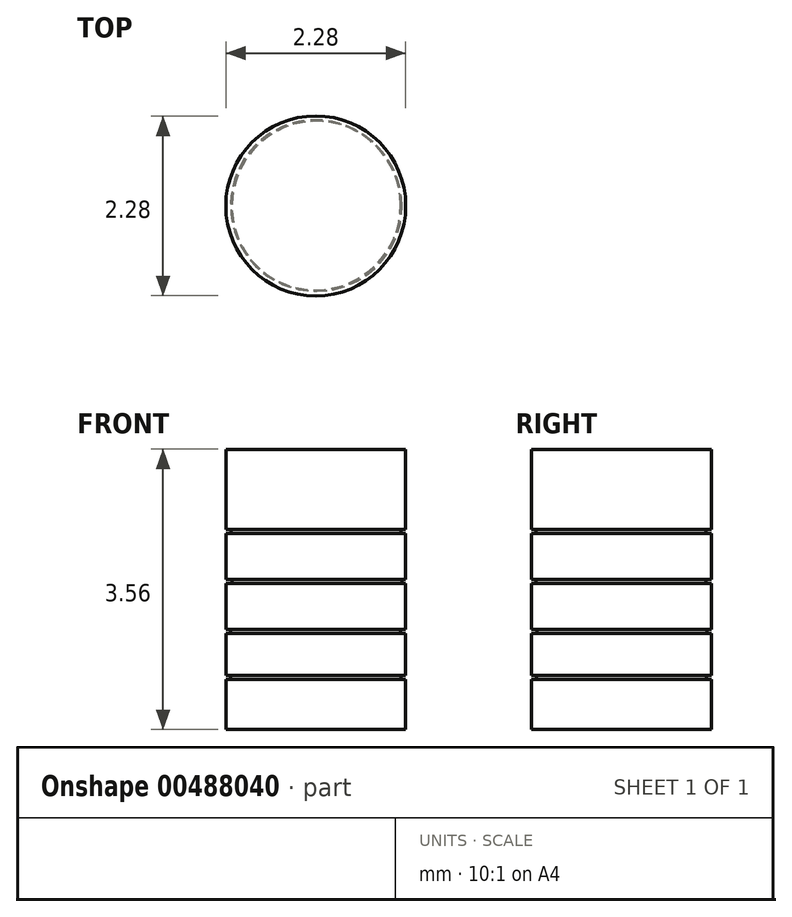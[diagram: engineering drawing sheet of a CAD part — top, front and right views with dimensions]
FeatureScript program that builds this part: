
annotation { "Feature Type Name" : "Feature", "Feature Type Description" : "" }
export const myFeature = defineFeature(function(context is Context, id is Id, definition is map)
    precondition{}
    {
        {
            var Q0;
            Q0=qCreatedBy(makeId("Top.planeOp"),FACE);
            var sketch = newSketch(context, id + "F0", { "sketchPlane" : qUnion([Q0])});
            skCircle(sketch, "E0", {"center": v(0, 0) * mm, "radius": 1.14 * mm});
            skSolve(sketch);
        }
        {
            var Q0;
            Q0 = qSketchRegion(id + "F0", true);
            extrude(context, id + "F1", {"entities" : qUnion([Q0]), "depth" : 3.56 * mm, "offsetDistance" : 25.4 * mm});
        }
        {
            var Q0;
            Q0=qCreatedBy(makeId("Top.planeOp"),FACE);
            cPlane(context, id + "F2", {"entities" : qUnion([Q0]), "cplaneType" : CPlaneType.OFFSET, "offset" : 0.64 * mm, "width" : 152.4 * mm, "height" : 152.4 * mm});
        }
        {
            var Q0;
            Q0=qCreatedBy(id+"F2.planeOp",FACE);
            cPlane(context, id + "F3", {"entities" : qUnion([Q0]), "cplaneType" : CPlaneType.OFFSET, "offset" : 0.64 * mm, "width" : 152.4 * mm, "height" : 152.4 * mm});
        }
        {
            var Q0;
            Q0=qCreatedBy(id+"F3.planeOp",FACE);
            cPlane(context, id + "F4", {"entities" : qUnion([Q0]), "cplaneType" : CPlaneType.OFFSET, "offset" : 0.64 * mm, "width" : 152.4 * mm, "height" : 152.4 * mm});
        }
        {
            var Q0;
            Q0=qCreatedBy(id+"F4.planeOp",FACE);
            cPlane(context, id + "F5", {"entities" : qUnion([Q0]), "cplaneType" : CPlaneType.OFFSET, "offset" : 0.64 * mm, "width" : 152.4 * mm, "height" : 152.4 * mm});
        }
        {
            var Q0;
            Q0=qCreatedBy(id+"F2.planeOp",FACE);
            var sketch = newSketch(context, id + "F6", { "sketchPlane" : qUnion([Q0])});
            skCircle(sketch, "E1", {"center": v(0, 0) * mm, "radius": 1.08 * mm});
            skCircle(sketch, "E2", {"center": v(0, 0) * mm, "radius": 1.14 * mm});
            skSolve(sketch);
        }
        {
            var Q0;
            Q0 = qSketchRegion(id + "F6", true);
            extrude(context, id + "F7", {"entities" : qUnion([Q0]), "operationType" : NewBodyOperationType.REMOVE, "depth" : 0.05 * mm, "offsetDistance" : 25.4 * mm});
        }
        {
            var Q0;
            Q0=qCreatedBy(id+"F3.planeOp",FACE);
            var sketch = newSketch(context, id + "F8", { "sketchPlane" : qUnion([Q0])});
            skCircle(sketch, "E3", {"center": v(0, 0.01) * mm, "radius": 1.08 * mm});
            skCircle(sketch, "E4", {"center": v(0, 0.01) * mm, "radius": 1.16 * mm});
            skSolve(sketch);
        }
        {
            var Q0;
            Q0 = qSketchRegion(id + "F8", true);
            var Q1;
            Q1 = qConstructionFilter(qBodyType(qCreatedBy(id + "F8" ,EDGE), BodyType.WIRE), ConstructionObject.NO);
            extrude(context, id + "F9", {"entities" : qUnion([Q0]), "operationType" : NewBodyOperationType.REMOVE, "surfaceEntities" : qUnion([Q1]), "oppositeDirection" : true, "depth" : 0.05 * mm, "offsetDistance" : 25.4 * mm});
        }
        {
            var Q0;
            Q0=qCreatedBy(id+"F4.planeOp",FACE);
            var sketch = newSketch(context, id + "F10", { "sketchPlane" : qUnion([Q0])});
            skCircle(sketch, "E5", {"center": v(0.02, 0) * mm, "radius": 1.08 * mm});
            skCircle(sketch, "E6", {"center": v(0.02, 0) * mm, "radius": 1.17 * mm});
            skSolve(sketch);
        }
        {
            var Q0;
            Q0 = qSketchRegion(id + "F10", true);
            extrude(context, id + "F11", {"entities" : qUnion([Q0]), "operationType" : NewBodyOperationType.REMOVE, "oppositeDirection" : true, "depth" : 0.05 * mm, "offsetDistance" : 25.4 * mm});
        }
        {
            var Q0;
            Q0=qCreatedBy(id+"F5.planeOp",FACE);
            var sketch = newSketch(context, id + "F12", { "sketchPlane" : qUnion([Q0])});
            skCircle(sketch, "E7", {"center": v(0, 0) * mm, "radius": 1.08 * mm});
            skCircle(sketch, "E8", {"center": v(0, 0) * mm, "radius": 1.16 * mm});
            skSolve(sketch);
        }
        {
            var Q0;
            Q0 = qSketchRegion(id + "F12", true);
            var Q1;
            Q1 = qConstructionFilter(qBodyType(qCreatedBy(id + "F12" ,EDGE), BodyType.WIRE), ConstructionObject.NO);
            extrude(context, id + "F13", {"entities" : qUnion([Q0]), "operationType" : NewBodyOperationType.REMOVE, "surfaceEntities" : qUnion([Q1]), "oppositeDirection" : true, "depth" : 0.05 * mm, "offsetDistance" : 25.4 * mm});
        }
    });
